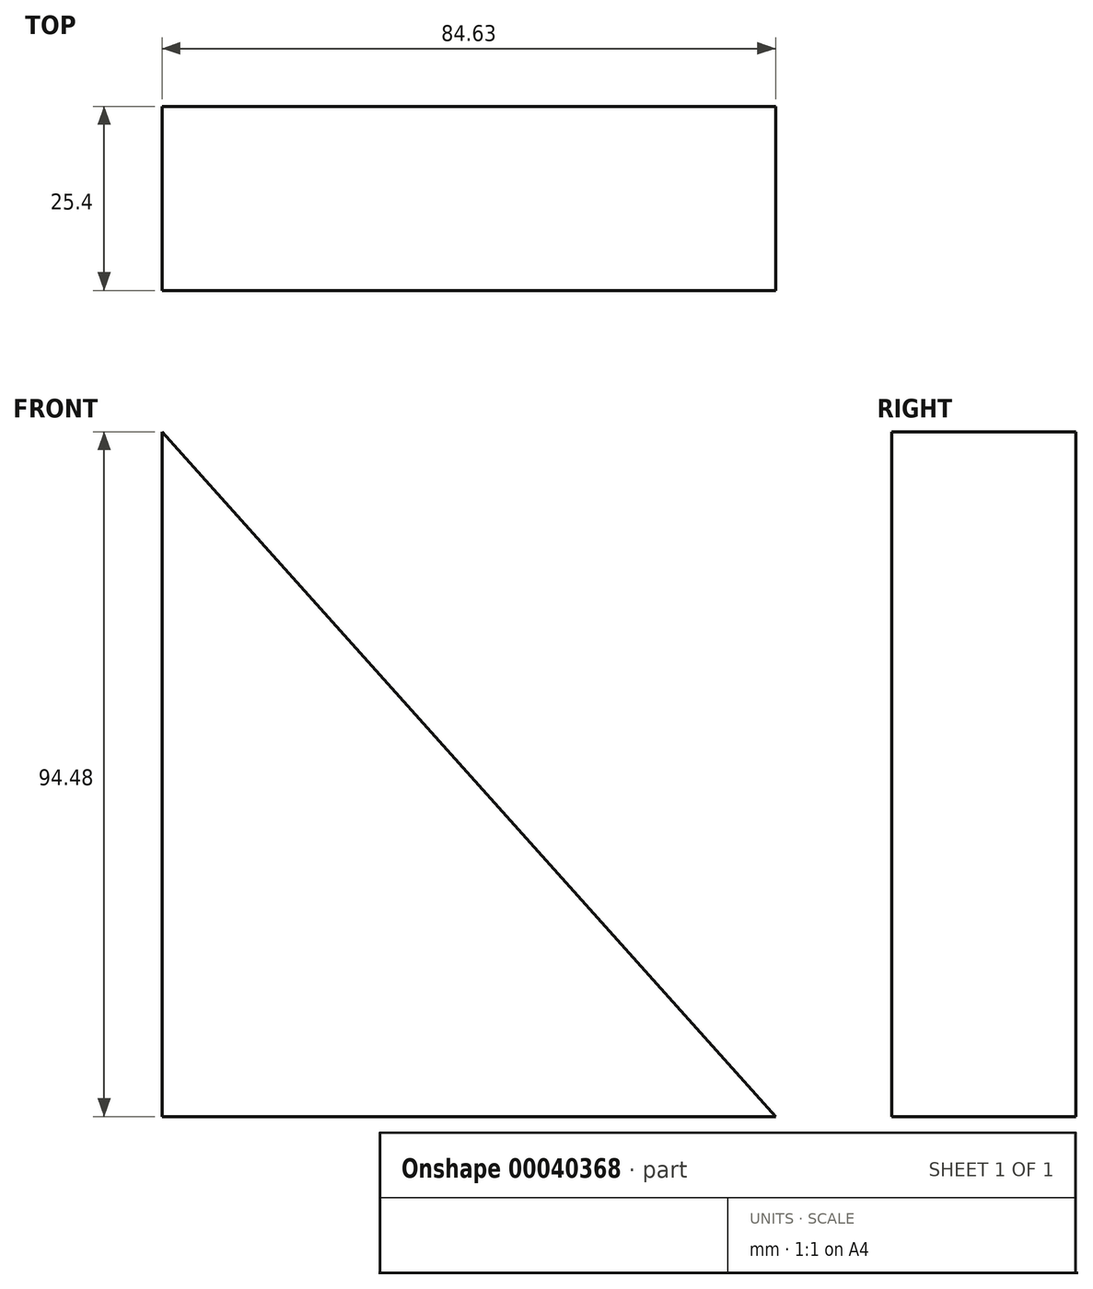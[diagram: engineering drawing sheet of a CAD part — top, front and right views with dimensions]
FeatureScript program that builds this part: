
annotation { "Feature Type Name" : "Feature", "Feature Type Description" : "" }
export const myFeature = defineFeature(function(context is Context, id is Id, definition is map)
    precondition{}
    {
        {
            var Q0;
            Q0=qCreatedBy(makeId("Front.planeOp"),FACE);
            var sketch = newSketch(context, id + "F0", { "sketchPlane" : qUnion([Q0])});
            skLineSegment(sketch, "E0", {"start": v(-41.92, 52.06) * mm, "end": v(-41.92, -42.42) * mm});
            skLineSegment(sketch, "E1", {"start": v(-41.92, -42.42) * mm, "end": v(42.71, -42.42) * mm});
            skLineSegment(sketch, "E2", {"start": v(42.71, -42.42) * mm, "end": v(-41.92, 52.06) * mm});
            skLineSegment(sketch, "E3", {"start": v(-41.92, 52.06) * mm, "end": v(46.45, 52.06) * mm});
            skSolve(sketch);
        }
        {
            var Q0;
            Q0=makeQuery(id+"F0.imprint","IMPRINT",FACE,{"disambiguationData":[TD([[makeQuery(id+"F0.imprint","IMPRINT",EDGE,{"derivedFrom":sQuery(id+"F0.wireOp",EDGE,"E0")}),1.0]])]});
            extrude(context, id + "F1", {"entities" : qUnion([Q0]), "depth" : 25.4 * mm});
        }
    });
